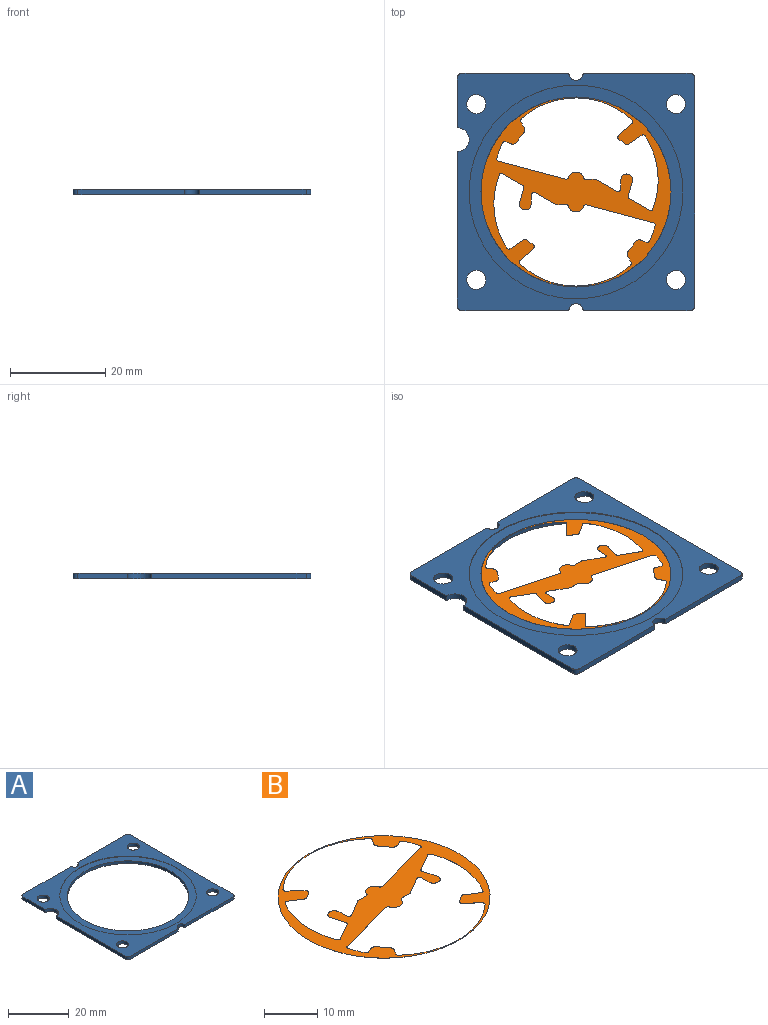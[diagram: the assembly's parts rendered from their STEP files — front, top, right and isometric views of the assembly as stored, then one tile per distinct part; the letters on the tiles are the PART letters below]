
ASSEMBLY  parts=2 mates=1
PART A: 23 faces, bbox 50x50x1.2 mm
  f0: plane 48x1.2mm, normal (1,0,0), area 57.6mm2, adj f1,f17,f18,f19
  f1: cylinder r=1mm len=1.2mm, axis (0,0,-1), area 1.9mm2, adj f0,f2,f18,f19
  f2: plane 22.5x1.2mm, normal (0,1,0), area 27mm2, adj f1,f3,f18,f19
  f3: cylinder r=1.5mm len=3mm, axis (0,0,-1), area 5.7mm2, adj f2,f4,f18,f19
  f4: plane 22.5x1.2mm, normal (0,1,0), area 27mm2, adj f3,f5,f18,f19
  f5: cylinder r=1mm len=1.2mm, axis (0,0,-1), area 1.9mm2, adj f4,f6,f18,f19
  f6: plane 10.5x1.2mm, normal (-1,0,0), area 12.6mm2, adj f5,f7,f18,f19
  f7: cylinder r=2.5mm len=5mm, axis (0,0,-1), area 9.4mm2, adj f6,f8,f18,f19
  f8: plane 32.5x1.2mm, normal (-1,0,0), area 39mm2, adj f7,f9,f18,f19
  f9: cylinder r=1mm len=1.2mm, axis (0,0,-1), area 1.9mm2, adj f8,f10,f18,f19
  f10: plane 22.5x1.2mm, normal (0,-1,0), area 27mm2, adj f9,f11,f18,f19
  f11: cylinder r=1.5mm len=3mm, axis (0,0,-1), area 5.7mm2, adj f10,f12,f18,f19
  f12: plane 22.5x1.2mm, normal (0,-1,0), area 27mm2, adj f11,f17,f18,f19
  f13: cylinder r=2mm len=4.01mm, axis (0,0,-1), area 15.1mm2, adj f18,f19
  f14: cylinder r=2mm len=4.01mm, axis (0,0,-1), area 15.1mm2, adj f18,f19
  f15: cylinder r=2mm len=4.01mm, axis (0,0,-1), area 15.1mm2, adj f18,f19
  f16: cylinder r=2mm len=4.01mm, axis (0,0,-1), area 15.1mm2, adj f18,f19
  f17: cylinder r=1mm len=1.2mm, axis (0,0,-1), area 1.9mm2, adj f0,f12,f18,f19
  f18: plane 50x50mm, normal (0,0,1), area 841.3mm2, adj f0,f1,f2,f3,f4,f5,f6,f7
  f19: plane 50x50mm, normal (0,0,-1), area 1175.1mm2, adj f0,f1,f2,f3,f4,f5,f6,f7
  f20: cylinder r=22.5mm len=45mm, axis (0,0,1), area 22.6mm2, adj f18,f21
  f21: plane 45x45mm, normal (0,0,1), area 333.8mm2, adj f20,f22
  f22: cylinder r=20mm len=40mm, axis (0,0,-1), area 130.7mm2, adj f19,f21
PART B: 67 faces, bbox 40x40x0 mm
  f0: cylinder r=17.3mm len=23.28mm, axis (0,0,-1), area 0.3mm2, adj f1,f62,f65,f66
  f1: cylinder r=0.5mm len=0.64mm, axis (0,0,-1), area 0mm2, adj f0,f2,f65,f66
  f2: plane 1.11x0.7mm, normal (0.85,-0.53,0), area 0mm2, adj f1,f3,f65,f66
  f3: cylinder r=1mm len=1.14mm, axis (0,0,-1), area 0mm2, adj f2,f4,f65,f66
  f4: plane 2.04x1.55mm, normal (0.8,0.61,0), area 0mm2, adj f3,f5,f65,f66
  f5: cylinder r=1mm len=1.21mm, axis (0,0,-1), area 0mm2, adj f4,f6,f65,f66
  f6: plane 1.02x0.46mm, normal (-0.41,0.91,0), area 0mm2, adj f5,f7,f65,f66
  f7: cylinder r=0.5mm len=0.65mm, axis (0,0,-1), area 0mm2, adj f6,f8,f65,f66
  f8: cylinder r=17.3mm len=3.29mm, axis (0,0,-1), area 0mm2, adj f7,f9,f65,f66
  f9: cylinder r=0.5mm len=0.62mm, axis (0,0,-1), area 0mm2, adj f8,f10,f65,f66
  f10: plane 14.11x3.78mm, normal (0.26,-0.97,0), area 0.1mm2, adj f9,f11,f65,f66
  f11: cylinder r=0.5mm len=0.6mm, axis (0,0,-1), area 0mm2, adj f10,f12,f65,f66
  f12: cylinder r=1.7mm len=3.24mm, axis (0,0,-1), area 0mm2, adj f11,f13,f65,f66
  f13: cylinder r=0.5mm len=0.48mm, axis (0,0,-1), area 0mm2, adj f12,f14,f65,f66
  f14: plane 1.9x0.01mm, normal (0,-1,0), area 0mm2, adj f13,f15,f65,f66
  f15: cylinder r=1mm len=0.5mm, axis (0,0,-1), area 0mm2, adj f14,f16,f65,f66
  f16: plane 4.11x2.37mm, normal (0.5,-0.87,0), area 0mm2, adj f15,f17,f65,f66
  f17: cylinder r=0.5mm len=0.75mm, axis (0,0,-1), area 0mm2, adj f16,f18,f65,f66
  f18: plane 2.03x0.07mm, normal (-1,-0.04,0), area 0mm2, adj f17,f19,f65,f66
  f19: cylinder r=1.25mm len=2.5mm, axis (0,0,-1), area 0mm2, adj f18,f20,f65,f66
  f20: plane 2.98x0.88mm, normal (0.96,0.28,0), area 0mm2, adj f19,f21,f65,f66
  f21: cylinder r=0.5mm len=0.57mm, axis (0,0,-1), area 0mm2, adj f20,f22,f65,f66
  f22: plane 4.25x2.45mm, normal (0.5,-0.87,0), area 0mm2, adj f21,f23,f65,f66
  f23: cylinder r=0.5mm len=0.72mm, axis (0,0,-1), area 0mm2, adj f22,f24,f65,f66
  f24: cylinder r=17.3mm len=15.37mm, axis (0,0,-1), area 0.2mm2, adj f23,f25,f65,f66
  f25: cylinder r=0.5mm len=0.69mm, axis (0,0,-1), area 0mm2, adj f24,f26,f65,f66
  f26: plane 2.88x1.87mm, normal (0.54,0.84,0), area 0mm2, adj f25,f27,f65,f66
  f27: cylinder r=0.5mm len=0.55mm, axis (0,0,-1), area 0mm2, adj f26,f28,f65,f66
  f28: plane 1.45x0.99mm, normal (-0.56,0.83,0), area 0mm2, adj f27,f29,f65,f66
  f29: cylinder r=0.5mm len=0.78mm, axis (0,0,-1), area 0mm2, adj f28,f30,f65,f66
  f30: plane 2.8x2.61mm, normal (-0.68,-0.73,0), area 0mm2, adj f29,f62,f65,f66
  f31: cylinder r=17.3mm len=23.28mm, axis (0,0,-1), area 0.3mm2, adj f32,f63,f65,f66
  f32: cylinder r=0.5mm len=0.64mm, axis (0,0,-1), area 0mm2, adj f31,f33,f65,f66
  f33: plane 1.11x0.7mm, normal (-0.85,0.53,0), area 0mm2, adj f32,f34,f65,f66
  f34: cylinder r=1mm len=1.14mm, axis (0,0,-1), area 0mm2, adj f33,f35,f65,f66
  f35: plane 2.04x1.55mm, normal (-0.8,-0.61,0), area 0mm2, adj f34,f36,f65,f66
  f36: cylinder r=1mm len=1.21mm, axis (0,0,-1), area 0mm2, adj f35,f37,f65,f66
  f37: plane 1.02x0.46mm, normal (0.41,-0.91,0), area 0mm2, adj f36,f38,f65,f66
  f38: cylinder r=0.5mm len=0.65mm, axis (0,0,-1), area 0mm2, adj f37,f39,f65,f66
  f39: cylinder r=17.3mm len=3.29mm, axis (0,0,-1), area 0mm2, adj f38,f40,f65,f66
  f40: cylinder r=0.5mm len=0.62mm, axis (0,0,-1), area 0mm2, adj f39,f41,f65,f66
  f41: plane 14.11x3.78mm, normal (-0.26,0.97,0), area 0.1mm2, adj f40,f42,f65,f66
  f42: cylinder r=0.5mm len=0.6mm, axis (0,0,-1), area 0mm2, adj f41,f43,f65,f66
  f43: cylinder r=1.7mm len=3.24mm, axis (0,0,-1), area 0mm2, adj f42,f44,f65,f66
  f44: cylinder r=0.5mm len=0.48mm, axis (0,0,-1), area 0mm2, adj f43,f45,f65,f66
  f45: plane 1.9x0.01mm, normal (0,1,0), area 0mm2, adj f44,f46,f65,f66
  f46: cylinder r=1mm len=0.5mm, axis (0,0,-1), area 0mm2, adj f45,f47,f65,f66
  f47: plane 4.11x2.37mm, normal (-0.5,0.87,0), area 0mm2, adj f46,f48,f65,f66
  f48: cylinder r=0.5mm len=0.75mm, axis (0,0,-1), area 0mm2, adj f47,f49,f65,f66
  f49: plane 2.03x0.07mm, normal (1,0.04,0), area 0mm2, adj f48,f50,f65,f66
  f50: cylinder r=1.25mm len=2.5mm, axis (0,0,-1), area 0mm2, adj f49,f51,f65,f66
  f51: plane 2.98x0.88mm, normal (-0.96,-0.28,0), area 0mm2, adj f50,f52,f65,f66
  f52: cylinder r=0.5mm len=0.57mm, axis (0,0,-1), area 0mm2, adj f51,f53,f65,f66
  f53: plane 4.25x2.45mm, normal (-0.5,0.87,0), area 0mm2, adj f52,f54,f65,f66
  f54: cylinder r=0.5mm len=0.72mm, axis (0,0,-1), area 0mm2, adj f53,f55,f65,f66
  f55: cylinder r=17.3mm len=15.37mm, axis (0,0,-1), area 0.2mm2, adj f54,f56,f65,f66
  f56: cylinder r=0.5mm len=0.69mm, axis (0,0,-1), area 0mm2, adj f55,f57,f65,f66
  f57: plane 2.88x1.87mm, normal (-0.54,-0.84,0), area 0mm2, adj f56,f58,f65,f66
  f58: cylinder r=0.5mm len=0.55mm, axis (0,0,-1), area 0mm2, adj f57,f59,f65,f66
  f59: plane 1.45x0.99mm, normal (0.56,-0.83,0), area 0mm2, adj f58,f60,f65,f66
  f60: cylinder r=0.5mm len=0.78mm, axis (0,0,-1), area 0mm2, adj f59,f61,f65,f66
  f61: plane 2.8x2.61mm, normal (0.68,0.73,0), area 0mm2, adj f60,f63,f65,f66
  f62: cylinder r=0.5mm len=0.73mm, axis (0,0,-1), area 0mm2, adj f0,f30,f65,f66
  f63: cylinder r=0.5mm len=0.73mm, axis (0,0,-1), area 0mm2, adj f31,f61,f65,f66
  f64: cylinder r=20mm len=40mm, axis (0,0,-1), area 1.3mm2, adj f65,f66
  f65: plane 40x40mm, normal (0,0,1), area 375.4mm2, adj f0,f1,f2,f3,f4,f5,f6,f7
  f66: plane 40x40mm, normal (0,0,-1), area 375.4mm2, adj f0,f1,f2,f3,f4,f5,f6,f7
PLACE A at identity
PLACE B rot(axis=(1,0,0),180deg) t=(0,0,1.04)mm
MATE fastened B.f64 <-> A.f20  axis (0,0,1) through (0,0,1.04)mm
